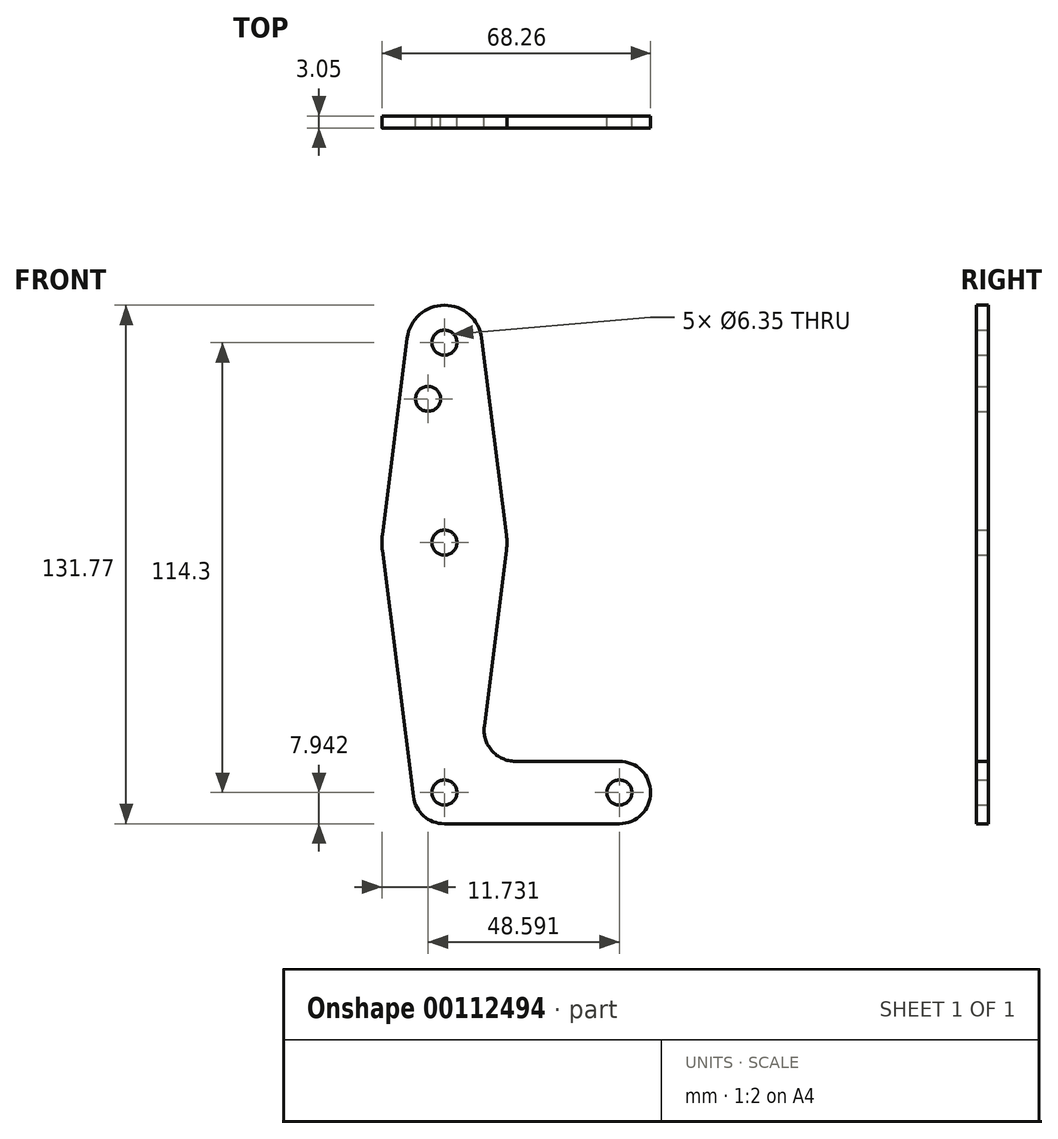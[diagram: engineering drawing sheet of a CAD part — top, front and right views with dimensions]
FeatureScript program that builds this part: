
annotation { "Feature Type Name" : "Feature", "Feature Type Description" : "" }
export const myFeature = defineFeature(function(context is Context, id is Id, definition is map)
    precondition{}
    {
        {
            var Q0;
            Q0=qCreatedBy(makeId("Front.planeOp"),FACE);
            var sketch = newSketch(context, id + "F0", { "sketchPlane" : qUnion([Q0])});
            skLineSegment(sketch, "E0", {"start": v(-23.5, 64.55) * mm, "end": v(-23.5, -49.75) * mm, "construction": true});
            skLineSegment(sketch, "E1", {"start": v(-23.5, -49.75) * mm, "end": v(20.94, -49.75) * mm});
            skCircle(sketch, "E2", {"center": v(-23.5, -49.75) * mm, "radius": 7.94 * mm});
            skCircle(sketch, "E3", {"center": v(20.94, -49.75) * mm, "radius": 7.94 * mm});
            skCircle(sketch, "E4", {"center": v(-23.5, 13.75) * mm, "radius": 15.88 * mm});
            skCircle(sketch, "E5", {"center": v(-23.5, 64.55) * mm, "radius": 9.52 * mm});
            skLineSegment(sketch, "E6", {"start": v(-5.5, -41.81) * mm, "end": v(20.94, -41.81) * mm});
            skLineSegment(sketch, "E7", {"start": v(-23.5, -57.69) * mm, "end": v(20.94, -57.69) * mm});
            skLineSegment(sketch, "E8", {"start": v(-14.06, 65.74) * mm, "end": v(-7.76, 15.74) * mm});
            skLineSegment(sketch, "E9", {"start": v(-32.96, 65.74) * mm, "end": v(-39.26, 15.74) * mm});
            skLineSegment(sketch, "E10", {"start": v(-39.26, 11.77) * mm, "end": v(-31.38, -50.74) * mm});
            skLineSegment(sketch, "E11", {"start": v(-7.76, 11.77) * mm, "end": v(-13.38, -32.87) * mm});
            skCircle(sketch, "E12", {"center": v(-23.5, 64.55) * mm, "radius": 3.18 * mm});
            skCircle(sketch, "E13", {"center": v(-23.5, 13.75) * mm, "radius": 3.18 * mm});
            skCircle(sketch, "E14", {"center": v(-23.5, -49.75) * mm, "radius": 3.18 * mm});
            skCircle(sketch, "E15", {"center": v(20.94, -49.75) * mm, "radius": 3.18 * mm});
            skCircle(sketch, "E16", {"center": v(-27.65, 50.28) * mm, "radius": 3.18 * mm});
            skArc(sketch, "E17.filletArc", {"start": v(-13.38, -32.87) * mm, "mid": v(-11.46, -39.12) * mm, "end": v(-5.5, -41.81) * mm});
            skSolve(sketch);
        }
        {
            var Q0;
            Q0 = qSketchRegion(id + "F0", true);
            extrude(context, id + "F1", {"entities" : qUnion([Q0]), "depth" : 3.05 * mm});
        }
    });
